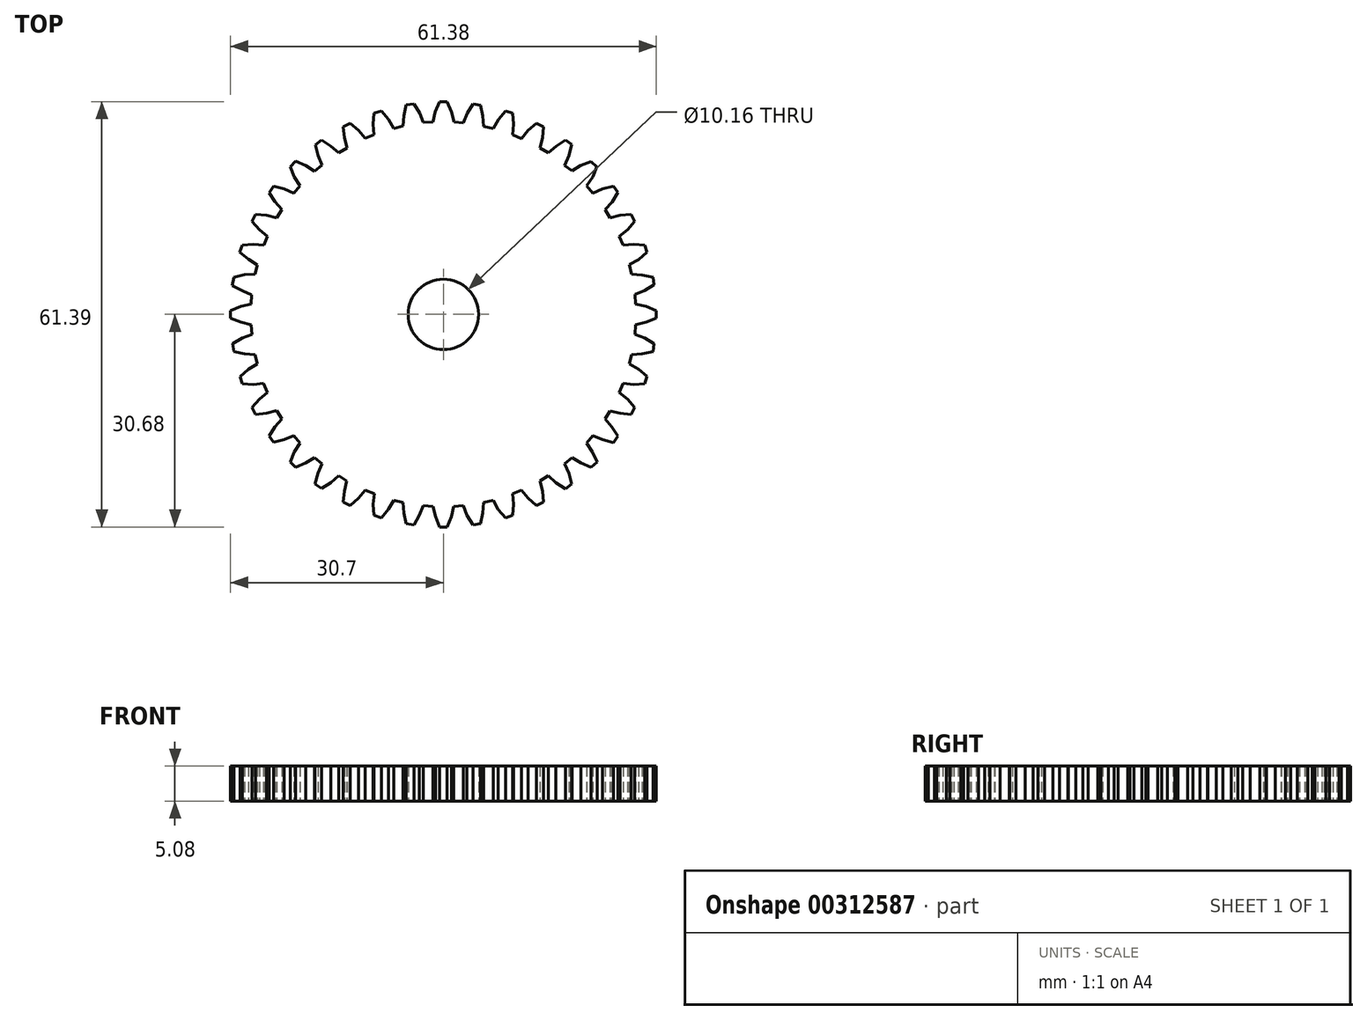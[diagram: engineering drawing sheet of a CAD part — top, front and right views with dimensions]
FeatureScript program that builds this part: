
annotation { "Feature Type Name" : "Feature", "Feature Type Description" : "" }
export const myFeature = defineFeature(function(context is Context, id is Id, definition is map)
    precondition{}
    {
        {
            var Q0;
            Q0=qCreatedBy(makeId("Top.planeOp"),FACE);
            var sketch = newSketch(context, id + "F0", { "sketchPlane" : qUnion([Q0])});
            skLineSegment(sketch, "E0", {"start": v(-21.5, -19.86) * mm, "end": v(-20.66, -18.56) * mm});
            skLineSegment(sketch, "E1", {"start": v(-20.66, -18.56) * mm, "end": v(-21.58, -17.48) * mm});
            skLineSegment(sketch, "E2", {"start": v(-21.58, -17.48) * mm, "end": v(-22.96, -18.1) * mm});
            skLineSegment(sketch, "E3", {"start": v(-22.96, -18.1) * mm, "end": v(-24.51, -18.48) * mm});
            skLineSegment(sketch, "E4", {"start": v(-24.51, -18.48) * mm, "end": v(-25.16, -17.59) * mm});
            skLineSegment(sketch, "E5", {"start": v(-25.16, -17.59) * mm, "end": v(-24.31, -16.23) * mm});
            skLineSegment(sketch, "E6", {"start": v(-24.31, -16.23) * mm, "end": v(-23.3, -15.1) * mm});
            skLineSegment(sketch, "E7", {"start": v(-23.3, -15.1) * mm, "end": v(-24.05, -13.9) * mm});
            skLineSegment(sketch, "E8", {"start": v(-24.05, -13.9) * mm, "end": v(-25.51, -14.28) * mm});
            skLineSegment(sketch, "E9", {"start": v(-25.51, -14.28) * mm, "end": v(-27.1, -14.42) * mm});
            skLineSegment(sketch, "E10", {"start": v(-27.1, -14.42) * mm, "end": v(-27.6, -13.44) * mm});
            skLineSegment(sketch, "E11", {"start": v(-27.6, -13.44) * mm, "end": v(-26.56, -12.22) * mm});
            skLineSegment(sketch, "E12", {"start": v(-26.56, -12.22) * mm, "end": v(-25.4, -11.3) * mm});
            skLineSegment(sketch, "E13", {"start": v(-25.4, -11.3) * mm, "end": v(-25.93, -9.96) * mm});
            skLineSegment(sketch, "E14", {"start": v(-25.93, -9.96) * mm, "end": v(-27.43, -10.11) * mm});
            skLineSegment(sketch, "E15", {"start": v(-27.43, -10.11) * mm, "end": v(-29.02, -10) * mm});
            skLineSegment(sketch, "E16", {"start": v(-29.02, -10) * mm, "end": v(-29.35, -8.98) * mm});
            skLineSegment(sketch, "E17", {"start": v(-29.35, -8.98) * mm, "end": v(-28.14, -7.93) * mm});
            skLineSegment(sketch, "E18", {"start": v(-28.14, -7.93) * mm, "end": v(-26.84, -7.16) * mm});
            skLineSegment(sketch, "E19", {"start": v(-26.84, -7.16) * mm, "end": v(-27.16, -5.79) * mm});
            skLineSegment(sketch, "E20", {"start": v(-27.16, -5.79) * mm, "end": v(-28.69, -5.68) * mm});
            skLineSegment(sketch, "E21", {"start": v(-28.69, -5.68) * mm, "end": v(-30.24, -5.35) * mm});
            skLineSegment(sketch, "E22", {"start": v(-30.24, -5.35) * mm, "end": v(-30.4, -4.24) * mm});
            skLineSegment(sketch, "E23", {"start": v(-30.4, -4.24) * mm, "end": v(-29.02, -3.43) * mm});
            skLineSegment(sketch, "E24", {"start": v(-29.02, -3.43) * mm, "end": v(-27.6, -2.86) * mm});
            skLineSegment(sketch, "E25", {"start": v(-27.6, -2.86) * mm, "end": v(-27.74, -1.46) * mm});
            skLineSegment(sketch, "E26", {"start": v(-27.74, -1.46) * mm, "end": v(-29.22, -1.14) * mm});
            skLineSegment(sketch, "E27", {"start": v(-29.22, -1.14) * mm, "end": v(-30.7, -0.55) * mm});
            skLineSegment(sketch, "E28", {"start": v(-30.7, -0.55) * mm, "end": v(-30.7, 0.57) * mm});
            skLineSegment(sketch, "E29", {"start": v(-30.7, 0.57) * mm, "end": v(-29.22, 1.16) * mm});
            skLineSegment(sketch, "E30", {"start": v(-29.22, 1.16) * mm, "end": v(-27.74, 1.5) * mm});
            skLineSegment(sketch, "E31", {"start": v(-27.74, 1.5) * mm, "end": v(-27.65, 2.82) * mm});
            skLineSegment(sketch, "E32", {"start": v(-27.65, 2.82) * mm, "end": v(-28.95, 3.4) * mm});
            skLineSegment(sketch, "E33", {"start": v(-28.95, 3.4) * mm, "end": v(-30.44, 4.17) * mm});
            skLineSegment(sketch, "E34", {"start": v(-30.44, 4.17) * mm, "end": v(-30.23, 5.36) * mm});
            skLineSegment(sketch, "E35", {"start": v(-30.23, 5.36) * mm, "end": v(-28.68, 5.72) * mm});
            skLineSegment(sketch, "E36", {"start": v(-28.68, 5.72) * mm, "end": v(-27.17, 5.8) * mm});
            skLineSegment(sketch, "E37", {"start": v(-27.17, 5.8) * mm, "end": v(-26.88, 7.15) * mm});
            skLineSegment(sketch, "E38", {"start": v(-26.88, 7.15) * mm, "end": v(-28.14, 7.95) * mm});
            skLineSegment(sketch, "E39", {"start": v(-28.14, 7.95) * mm, "end": v(-29.37, 8.97) * mm});
            skLineSegment(sketch, "E40", {"start": v(-29.37, 8.97) * mm, "end": v(-29.02, 10.02) * mm});
            skLineSegment(sketch, "E41", {"start": v(-29.02, 10.02) * mm, "end": v(-27.43, 10.13) * mm});
            skLineSegment(sketch, "E42", {"start": v(-27.43, 10.13) * mm, "end": v(-25.93, 9.98) * mm});
            skLineSegment(sketch, "E43", {"start": v(-25.93, 9.98) * mm, "end": v(-25.4, 11.3) * mm});
            skLineSegment(sketch, "E44", {"start": v(-25.4, 11.3) * mm, "end": v(-26.56, 12.25) * mm});
            skLineSegment(sketch, "E45", {"start": v(-26.56, 12.25) * mm, "end": v(-27.6, 13.45) * mm});
            skLineSegment(sketch, "E46", {"start": v(-27.6, 13.45) * mm, "end": v(-27.1, 14.42) * mm});
            skLineSegment(sketch, "E47", {"start": v(-27.1, 14.42) * mm, "end": v(-25.52, 14.32) * mm});
            skLineSegment(sketch, "E48", {"start": v(-25.52, 14.32) * mm, "end": v(-24.04, 13.92) * mm});
            skLineSegment(sketch, "E49", {"start": v(-24.04, 13.92) * mm, "end": v(-23.31, 15.12) * mm});
            skLineSegment(sketch, "E50", {"start": v(-23.31, 15.12) * mm, "end": v(-24.3, 16.26) * mm});
            skLineSegment(sketch, "E51", {"start": v(-24.3, 16.26) * mm, "end": v(-25.16, 17.59) * mm});
            skLineSegment(sketch, "E52", {"start": v(-25.16, 17.59) * mm, "end": v(-24.5, 18.5) * mm});
            skLineSegment(sketch, "E53", {"start": v(-24.5, 18.5) * mm, "end": v(-22.97, 18.11) * mm});
            skLineSegment(sketch, "E54", {"start": v(-22.97, 18.11) * mm, "end": v(-21.56, 17.49) * mm});
            skLineSegment(sketch, "E55", {"start": v(-21.56, 17.49) * mm, "end": v(-20.68, 18.58) * mm});
            skLineSegment(sketch, "E56", {"start": v(-20.68, 18.58) * mm, "end": v(-21.5, 19.85) * mm});
            skLineSegment(sketch, "E57", {"start": v(-21.5, 19.85) * mm, "end": v(-22.1, 21.31) * mm});
            skLineSegment(sketch, "E58", {"start": v(-22.1, 21.31) * mm, "end": v(-21.3, 22.11) * mm});
            skLineSegment(sketch, "E59", {"start": v(-21.3, 22.11) * mm, "end": v(-19.85, 21.48) * mm});
            skLineSegment(sketch, "E60", {"start": v(-19.85, 21.48) * mm, "end": v(-18.58, 20.66) * mm});
            skLineSegment(sketch, "E61", {"start": v(-18.58, 20.66) * mm, "end": v(-17.5, 21.58) * mm});
            skLineSegment(sketch, "E62", {"start": v(-17.5, 21.58) * mm, "end": v(-18.1, 22.97) * mm});
            skLineSegment(sketch, "E63", {"start": v(-18.1, 22.97) * mm, "end": v(-18.49, 24.5) * mm});
            skLineSegment(sketch, "E64", {"start": v(-18.49, 24.5) * mm, "end": v(-17.6, 25.17) * mm});
            skLineSegment(sketch, "E65", {"start": v(-17.6, 25.17) * mm, "end": v(-16.25, 24.32) * mm});
            skLineSegment(sketch, "E66", {"start": v(-16.25, 24.32) * mm, "end": v(-15.12, 23.32) * mm});
            skLineSegment(sketch, "E67", {"start": v(-15.12, 23.32) * mm, "end": v(-13.91, 24.05) * mm});
            skLineSegment(sketch, "E68", {"start": v(-13.91, 24.05) * mm, "end": v(-14.3, 25.52) * mm});
            skLineSegment(sketch, "E69", {"start": v(-14.3, 25.52) * mm, "end": v(-14.44, 27.1) * mm});
            skLineSegment(sketch, "E70", {"start": v(-14.44, 27.1) * mm, "end": v(-13.45, 27.6) * mm});
            skLineSegment(sketch, "E71", {"start": v(-13.45, 27.6) * mm, "end": v(-12.25, 26.55) * mm});
            skLineSegment(sketch, "E72", {"start": v(-12.25, 26.55) * mm, "end": v(-11.3, 25.4) * mm});
            skLineSegment(sketch, "E73", {"start": v(-11.3, 25.4) * mm, "end": v(-10, 25.94) * mm});
            skLineSegment(sketch, "E74", {"start": v(-10, 25.94) * mm, "end": v(-10.14, 27.45) * mm});
            skLineSegment(sketch, "E75", {"start": v(-10.14, 27.45) * mm, "end": v(-10.05, 29.03) * mm});
            skLineSegment(sketch, "E76", {"start": v(-10.05, 29.03) * mm, "end": v(-8.97, 29.37) * mm});
            skLineSegment(sketch, "E77", {"start": v(-8.97, 29.37) * mm, "end": v(-7.93, 28.13) * mm});
            skLineSegment(sketch, "E78", {"start": v(-7.93, 28.13) * mm, "end": v(-7.18, 26.85) * mm});
            skLineSegment(sketch, "E79", {"start": v(-7.18, 26.85) * mm, "end": v(-5.8, 27.2) * mm});
            skLineSegment(sketch, "E80", {"start": v(-5.8, 27.2) * mm, "end": v(-5.7, 28.69) * mm});
            skLineSegment(sketch, "E81", {"start": v(-5.7, 28.69) * mm, "end": v(-5.36, 30.23) * mm});
            skLineSegment(sketch, "E82", {"start": v(-5.36, 30.23) * mm, "end": v(-4.26, 30.4) * mm});
            skLineSegment(sketch, "E83", {"start": v(-4.26, 30.4) * mm, "end": v(-3.4, 29.07) * mm});
            skLineSegment(sketch, "E84", {"start": v(-3.4, 29.07) * mm, "end": v(-2.9, 27.7) * mm});
            skLineSegment(sketch, "E85", {"start": v(-2.9, 27.7) * mm, "end": v(-1.5, 27.75) * mm});
            skLineSegment(sketch, "E86", {"start": v(-1.5, 27.75) * mm, "end": v(-1.17, 29.23) * mm});
            skLineSegment(sketch, "E87", {"start": v(-1.17, 29.23) * mm, "end": v(-0.56, 30.7) * mm});
            skLineSegment(sketch, "E88", {"start": v(-0.56, 30.7) * mm, "end": v(0.55, 30.7) * mm});
            skLineSegment(sketch, "E89", {"start": v(0.55, 30.7) * mm, "end": v(1.14, 29.24) * mm});
            skLineSegment(sketch, "E90", {"start": v(1.14, 29.24) * mm, "end": v(1.51, 27.75) * mm});
            skLineSegment(sketch, "E91", {"start": v(1.51, 27.75) * mm, "end": v(2.88, 27.62) * mm});
            skLineSegment(sketch, "E92", {"start": v(2.88, 27.62) * mm, "end": v(3.43, 29.04) * mm});
            skLineSegment(sketch, "E93", {"start": v(3.43, 29.04) * mm, "end": v(4.26, 30.4) * mm});
            skLineSegment(sketch, "E94", {"start": v(4.26, 30.4) * mm, "end": v(5.36, 30.22) * mm});
            skLineSegment(sketch, "E95", {"start": v(5.36, 30.22) * mm, "end": v(5.7, 28.68) * mm});
            skLineSegment(sketch, "E96", {"start": v(5.7, 28.68) * mm, "end": v(5.78, 27.17) * mm});
            skLineSegment(sketch, "E97", {"start": v(5.78, 27.17) * mm, "end": v(7.16, 26.85) * mm});
            skLineSegment(sketch, "E98", {"start": v(7.16, 26.85) * mm, "end": v(7.93, 28.14) * mm});
            skLineSegment(sketch, "E99", {"start": v(7.93, 28.14) * mm, "end": v(8.95, 29.37) * mm});
            skLineSegment(sketch, "E100", {"start": v(8.95, 29.37) * mm, "end": v(10, 29.02) * mm});
            skLineSegment(sketch, "E101", {"start": v(10, 29.02) * mm, "end": v(10.11, 27.43) * mm});
            skLineSegment(sketch, "E102", {"start": v(10.11, 27.43) * mm, "end": v(9.97, 25.94) * mm});
            skLineSegment(sketch, "E103", {"start": v(9.97, 25.94) * mm, "end": v(11.27, 25.39) * mm});
            skLineSegment(sketch, "E104", {"start": v(11.27, 25.39) * mm, "end": v(12.23, 26.55) * mm});
            skLineSegment(sketch, "E105", {"start": v(12.23, 26.55) * mm, "end": v(13.43, 27.6) * mm});
            skLineSegment(sketch, "E106", {"start": v(13.43, 27.6) * mm, "end": v(14.42, 27.1) * mm});
            skLineSegment(sketch, "E107", {"start": v(14.42, 27.1) * mm, "end": v(14.28, 25.52) * mm});
            skLineSegment(sketch, "E108", {"start": v(14.28, 25.52) * mm, "end": v(13.9, 24.05) * mm});
            skLineSegment(sketch, "E109", {"start": v(13.9, 24.05) * mm, "end": v(15.1, 23.31) * mm});
            skLineSegment(sketch, "E110", {"start": v(15.1, 23.31) * mm, "end": v(16.25, 24.31) * mm});
            skLineSegment(sketch, "E111", {"start": v(16.25, 24.31) * mm, "end": v(17.57, 25.16) * mm});
            skLineSegment(sketch, "E112", {"start": v(17.57, 25.16) * mm, "end": v(18.48, 24.51) * mm});
            skLineSegment(sketch, "E113", {"start": v(18.48, 24.51) * mm, "end": v(18.12, 22.97) * mm});
            skLineSegment(sketch, "E114", {"start": v(18.12, 22.97) * mm, "end": v(17.5, 21.48) * mm});
            skLineSegment(sketch, "E115", {"start": v(17.5, 21.48) * mm, "end": v(18.56, 20.72) * mm});
            skLineSegment(sketch, "E116", {"start": v(18.56, 20.72) * mm, "end": v(19.74, 21.48) * mm});
            skLineSegment(sketch, "E117", {"start": v(19.74, 21.48) * mm, "end": v(21.27, 22.07) * mm});
            skLineSegment(sketch, "E118", {"start": v(21.27, 22.07) * mm, "end": v(22.14, 21.3) * mm});
            skLineSegment(sketch, "E119", {"start": v(22.14, 21.3) * mm, "end": v(21.53, 19.85) * mm});
            skLineSegment(sketch, "E120", {"start": v(21.53, 19.85) * mm, "end": v(20.68, 18.56) * mm});
            skLineSegment(sketch, "E121", {"start": v(20.68, 18.56) * mm, "end": v(21.56, 17.5) * mm});
            skLineSegment(sketch, "E122", {"start": v(21.56, 17.5) * mm, "end": v(22.95, 18.1) * mm});
            skLineSegment(sketch, "E123", {"start": v(22.95, 18.1) * mm, "end": v(24.5, 18.5) * mm});
            skLineSegment(sketch, "E124", {"start": v(24.5, 18.5) * mm, "end": v(25.15, 17.6) * mm});
            skLineSegment(sketch, "E125", {"start": v(25.15, 17.6) * mm, "end": v(24.3, 16.24) * mm});
            skLineSegment(sketch, "E126", {"start": v(24.3, 16.24) * mm, "end": v(23.3, 15.12) * mm});
            skLineSegment(sketch, "E127", {"start": v(23.3, 15.12) * mm, "end": v(24.02, 13.92) * mm});
            skLineSegment(sketch, "E128", {"start": v(24.02, 13.92) * mm, "end": v(25.5, 14.3) * mm});
            skLineSegment(sketch, "E129", {"start": v(25.5, 14.3) * mm, "end": v(27.08, 14.44) * mm});
            skLineSegment(sketch, "E130", {"start": v(27.08, 14.44) * mm, "end": v(27.59, 13.45) * mm});
            skLineSegment(sketch, "E131", {"start": v(27.59, 13.45) * mm, "end": v(26.54, 12.25) * mm});
            skLineSegment(sketch, "E132", {"start": v(26.54, 12.25) * mm, "end": v(25.37, 11.3) * mm});
            skLineSegment(sketch, "E133", {"start": v(25.37, 11.3) * mm, "end": v(25.9, 9.98) * mm});
            skLineSegment(sketch, "E134", {"start": v(-21.5, -19.86) * mm, "end": v(-22.1, -21.3) * mm});
            skLineSegment(sketch, "E135", {"start": v(-22.1, -21.3) * mm, "end": v(-21.33, -22.08) * mm});
            skLineSegment(sketch, "E136", {"start": v(-21.33, -22.08) * mm, "end": v(-19.84, -21.46) * mm});
            skLineSegment(sketch, "E137", {"start": v(-19.84, -21.46) * mm, "end": v(-18.6, -20.68) * mm});
            skLineSegment(sketch, "E138", {"start": v(-18.06, -22.9) * mm, "end": v(-18.5, -24.49) * mm});
            skLineSegment(sketch, "E139", {"start": v(-18.5, -24.49) * mm, "end": v(-17.58, -25.13) * mm});
            skLineSegment(sketch, "E140", {"start": v(-17.58, -25.13) * mm, "end": v(-16.24, -24.31) * mm});
            skLineSegment(sketch, "E141", {"start": v(-16.24, -24.31) * mm, "end": v(-15.1, -23.3) * mm});
            skLineSegment(sketch, "E142", {"start": v(-15.1, -23.3) * mm, "end": v(-13.93, -24.04) * mm});
            skLineSegment(sketch, "E143", {"start": v(-13.93, -24.04) * mm, "end": v(-14.3, -25.5) * mm});
            skLineSegment(sketch, "E144", {"start": v(-14.3, -25.5) * mm, "end": v(-14.45, -27.07) * mm});
            skLineSegment(sketch, "E145", {"start": v(-14.45, -27.07) * mm, "end": v(-13.45, -27.6) * mm});
            skLineSegment(sketch, "E146", {"start": v(-13.45, -27.6) * mm, "end": v(-12.26, -26.53) * mm});
            skLineSegment(sketch, "E147", {"start": v(-12.26, -26.53) * mm, "end": v(-11.28, -25.39) * mm});
            skLineSegment(sketch, "E148", {"start": v(-11.28, -25.39) * mm, "end": v(-9.98, -25.9) * mm});
            skLineSegment(sketch, "E149", {"start": v(-9.98, -25.9) * mm, "end": v(-10.13, -27.4) * mm});
            skLineSegment(sketch, "E150", {"start": v(-10.13, -27.4) * mm, "end": v(-10.03, -29) * mm});
            skLineSegment(sketch, "E151", {"start": v(-10.03, -29) * mm, "end": v(-8.96, -29.35) * mm});
            skLineSegment(sketch, "E152", {"start": v(-8.96, -29.35) * mm, "end": v(-7.94, -28.13) * mm});
            skLineSegment(sketch, "E153", {"start": v(-7.94, -28.13) * mm, "end": v(-7.18, -26.82) * mm});
            skLineSegment(sketch, "E154", {"start": v(-7.18, -26.82) * mm, "end": v(-5.8, -27.15) * mm});
            skLineSegment(sketch, "E155", {"start": v(-5.8, -27.15) * mm, "end": v(-5.71, -28.66) * mm});
            skLineSegment(sketch, "E156", {"start": v(-5.71, -28.66) * mm, "end": v(-5.36, -30.21) * mm});
            skLineSegment(sketch, "E157", {"start": v(-5.36, -30.21) * mm, "end": v(-4.26, -30.4) * mm});
            skLineSegment(sketch, "E158", {"start": v(-4.26, -30.4) * mm, "end": v(-3.45, -29) * mm});
            skLineSegment(sketch, "E159", {"start": v(-3.45, -29) * mm, "end": v(-2.9, -27.6) * mm});
            skLineSegment(sketch, "E160", {"start": v(-2.9, -27.6) * mm, "end": v(-1.48, -27.72) * mm});
            skLineSegment(sketch, "E161", {"start": v(-1.48, -27.72) * mm, "end": v(-1.16, -29.2) * mm});
            skLineSegment(sketch, "E162", {"start": v(-1.16, -29.2) * mm, "end": v(-0.55, -30.68) * mm});
            skLineSegment(sketch, "E163", {"start": v(-0.55, -30.68) * mm, "end": v(0.54, -30.68) * mm});
            skLineSegment(sketch, "E164", {"start": v(0.54, -30.68) * mm, "end": v(1.14, -29.2) * mm});
            skLineSegment(sketch, "E165", {"start": v(1.14, -29.2) * mm, "end": v(1.47, -27.72) * mm});
            skLineSegment(sketch, "E166", {"start": v(1.47, -27.72) * mm, "end": v(2.86, -27.62) * mm});
            skLineSegment(sketch, "E167", {"start": v(2.86, -27.62) * mm, "end": v(3.4, -29) * mm});
            skLineSegment(sketch, "E168", {"start": v(3.4, -29) * mm, "end": v(4.26, -30.4) * mm});
            skLineSegment(sketch, "E169", {"start": v(4.26, -30.4) * mm, "end": v(5.35, -30.21) * mm});
            skLineSegment(sketch, "E170", {"start": v(5.35, -30.21) * mm, "end": v(5.69, -28.66) * mm});
            skLineSegment(sketch, "E171", {"start": v(5.69, -28.66) * mm, "end": v(5.78, -27.15) * mm});
            skLineSegment(sketch, "E172", {"start": v(5.78, -27.15) * mm, "end": v(7.16, -26.82) * mm});
            skLineSegment(sketch, "E173", {"start": v(7.16, -26.82) * mm, "end": v(7.92, -28.13) * mm});
            skLineSegment(sketch, "E174", {"start": v(7.92, -28.13) * mm, "end": v(8.95, -29.35) * mm});
            skLineSegment(sketch, "E175", {"start": v(8.95, -29.35) * mm, "end": v(10, -29) * mm});
            skLineSegment(sketch, "E176", {"start": v(10, -29) * mm, "end": v(10.1, -27.4) * mm});
            skLineSegment(sketch, "E177", {"start": v(10.1, -27.4) * mm, "end": v(9.98, -25.9) * mm});
            skLineSegment(sketch, "E178", {"start": v(9.98, -25.9) * mm, "end": v(11.27, -25.37) * mm});
            skLineSegment(sketch, "E179", {"start": v(11.27, -25.37) * mm, "end": v(12.22, -26.53) * mm});
            skLineSegment(sketch, "E180", {"start": v(12.22, -26.53) * mm, "end": v(13.43, -27.59) * mm});
            skLineSegment(sketch, "E181", {"start": v(13.43, -27.59) * mm, "end": v(14.42, -27.08) * mm});
            skLineSegment(sketch, "E182", {"start": v(14.42, -27.08) * mm, "end": v(14.28, -25.5) * mm});
            skLineSegment(sketch, "E183", {"start": v(14.28, -25.5) * mm, "end": v(13.9, -24.03) * mm});
            skLineSegment(sketch, "E184", {"start": v(13.9, -24.03) * mm, "end": v(15.1, -23.27) * mm});
            skLineSegment(sketch, "E185", {"start": v(15.1, -23.27) * mm, "end": v(16.23, -24.31) * mm});
            skLineSegment(sketch, "E186", {"start": v(16.23, -24.31) * mm, "end": v(17.58, -25.15) * mm});
            skLineSegment(sketch, "E187", {"start": v(17.58, -25.15) * mm, "end": v(18.48, -24.48) * mm});
            skLineSegment(sketch, "E188", {"start": v(18.48, -24.48) * mm, "end": v(18.1, -22.95) * mm});
            skLineSegment(sketch, "E189", {"start": v(18.1, -22.95) * mm, "end": v(17.5, -21.56) * mm});
            skLineSegment(sketch, "E190", {"start": v(17.5, -21.56) * mm, "end": v(18.56, -20.64) * mm});
            skLineSegment(sketch, "E191", {"start": v(18.56, -20.64) * mm, "end": v(19.84, -21.45) * mm});
            skLineSegment(sketch, "E192", {"start": v(19.84, -21.45) * mm, "end": v(21.3, -22.08) * mm});
            skLineSegment(sketch, "E193", {"start": v(21.3, -22.08) * mm, "end": v(22.18, -21.3) * mm});
            skLineSegment(sketch, "E194", {"start": v(22.18, -21.3) * mm, "end": v(21.47, -19.86) * mm});
            skLineSegment(sketch, "E195", {"start": v(21.47, -19.86) * mm, "end": v(20.65, -18.56) * mm});
            skLineSegment(sketch, "E196", {"start": v(20.65, -18.56) * mm, "end": v(21.56, -17.5) * mm});
            skLineSegment(sketch, "E197", {"start": v(21.56, -17.5) * mm, "end": v(22.94, -18.1) * mm});
            skLineSegment(sketch, "E198", {"start": v(22.94, -18.1) * mm, "end": v(24.5, -18.48) * mm});
            skLineSegment(sketch, "E199", {"start": v(24.5, -18.48) * mm, "end": v(25.14, -17.58) * mm});
            skLineSegment(sketch, "E200", {"start": v(25.14, -17.58) * mm, "end": v(24.3, -16.24) * mm});
            skLineSegment(sketch, "E201", {"start": v(24.3, -16.24) * mm, "end": v(23.3, -15.1) * mm});
            skLineSegment(sketch, "E202", {"start": v(23.3, -15.1) * mm, "end": v(24.03, -13.92) * mm});
            skLineSegment(sketch, "E203", {"start": v(24.03, -13.92) * mm, "end": v(25.49, -14.29) * mm});
            skLineSegment(sketch, "E204", {"start": v(25.49, -14.29) * mm, "end": v(27.08, -14.42) * mm});
            skLineSegment(sketch, "E205", {"start": v(27.08, -14.42) * mm, "end": v(27.59, -13.43) * mm});
            skLineSegment(sketch, "E206", {"start": v(27.59, -13.43) * mm, "end": v(26.54, -12.23) * mm});
            skLineSegment(sketch, "E207", {"start": v(26.54, -12.23) * mm, "end": v(25.37, -11.27) * mm});
            skLineSegment(sketch, "E208", {"start": v(25.37, -11.27) * mm, "end": v(25.91, -9.96) * mm});
            skLineSegment(sketch, "E209", {"start": v(25.91, -9.96) * mm, "end": v(27.42, -10.1) * mm});
            skLineSegment(sketch, "E210", {"start": v(27.42, -10.1) * mm, "end": v(29, -10) * mm});
            skLineSegment(sketch, "E211", {"start": v(29, -10) * mm, "end": v(29.35, -8.95) * mm});
            skLineSegment(sketch, "E212", {"start": v(29.35, -8.95) * mm, "end": v(28.13, -7.93) * mm});
            skLineSegment(sketch, "E213", {"start": v(28.13, -7.93) * mm, "end": v(26.82, -7.16) * mm});
            skLineSegment(sketch, "E214", {"start": v(26.82, -7.16) * mm, "end": v(27.15, -5.79) * mm});
            skLineSegment(sketch, "E215", {"start": v(27.15, -5.79) * mm, "end": v(28.66, -5.7) * mm});
            skLineSegment(sketch, "E216", {"start": v(28.66, -5.7) * mm, "end": v(30.21, -5.34) * mm});
            skLineSegment(sketch, "E217", {"start": v(30.21, -5.34) * mm, "end": v(30.4, -4.24) * mm});
            skLineSegment(sketch, "E218", {"start": v(30.4, -4.24) * mm, "end": v(29.02, -3.43) * mm});
            skLineSegment(sketch, "E219", {"start": v(29.02, -3.43) * mm, "end": v(27.61, -2.88) * mm});
            skLineSegment(sketch, "E220", {"start": v(27.61, -2.88) * mm, "end": v(27.72, -1.47) * mm});
            skLineSegment(sketch, "E221", {"start": v(27.72, -1.47) * mm, "end": v(29.2, -1.14) * mm});
            skLineSegment(sketch, "E222", {"start": v(29.2, -1.14) * mm, "end": v(30.68, -0.54) * mm});
            skLineSegment(sketch, "E223", {"start": v(30.68, -0.54) * mm, "end": v(30.68, 0.56) * mm});
            skLineSegment(sketch, "E224", {"start": v(30.68, 0.56) * mm, "end": v(29.2, 1.15) * mm});
            skLineSegment(sketch, "E225", {"start": v(29.2, 1.15) * mm, "end": v(27.73, 1.49) * mm});
            skLineSegment(sketch, "E226", {"start": v(27.73, 1.49) * mm, "end": v(27.6, 2.88) * mm});
            skLineSegment(sketch, "E227", {"start": v(27.6, 2.88) * mm, "end": v(29.02, 3.44) * mm});
            skLineSegment(sketch, "E228", {"start": v(29.02, 3.44) * mm, "end": v(30.4, 4.26) * mm});
            skLineSegment(sketch, "E229", {"start": v(30.4, 4.26) * mm, "end": v(30.22, 5.36) * mm});
            skLineSegment(sketch, "E230", {"start": v(30.22, 5.36) * mm, "end": v(28.66, 5.71) * mm});
            skLineSegment(sketch, "E231", {"start": v(28.66, 5.71) * mm, "end": v(27.15, 5.8) * mm});
            skLineSegment(sketch, "E232", {"start": v(27.15, 5.8) * mm, "end": v(26.82, 7.18) * mm});
            skLineSegment(sketch, "E233", {"start": v(26.82, 7.18) * mm, "end": v(28.13, 7.93) * mm});
            skLineSegment(sketch, "E234", {"start": v(28.13, 7.93) * mm, "end": v(29.34, 8.97) * mm});
            skLineSegment(sketch, "E235", {"start": v(29.34, 8.97) * mm, "end": v(29.02, 10.03) * mm});
            skLineSegment(sketch, "E236", {"start": v(29.02, 10.03) * mm, "end": v(27.42, 10.13) * mm});
            skLineSegment(sketch, "E237", {"start": v(27.42, 10.13) * mm, "end": v(25.9, 9.98) * mm});
            skLineSegment(sketch, "E238", {"start": v(-18.6, -20.68) * mm, "end": v(-17.5, -21.56) * mm});
            skLineSegment(sketch, "E239", {"start": v(-17.5, -21.56) * mm, "end": v(-18.06, -22.9) * mm});
            skCircle(sketch, "E240", {"center": v(0, 0) * mm, "radius": 5.08 * mm});
            skSolve(sketch);
        }
        {
            var Q0;
            Q0=makeQuery(id+"F0.imprint","IMPRINT",FACE,{"disambiguationData":[TD([[makeQuery(id+"F0.imprint","IMPRINT",EDGE,{"derivedFrom":sQuery(id+"F0.wireOp",EDGE,"E0")}),-1.0]])]});
            extrude(context, id + "F1", {"entities" : qUnion([Q0]), "depth" : 5.08 * mm});
        }
    });
